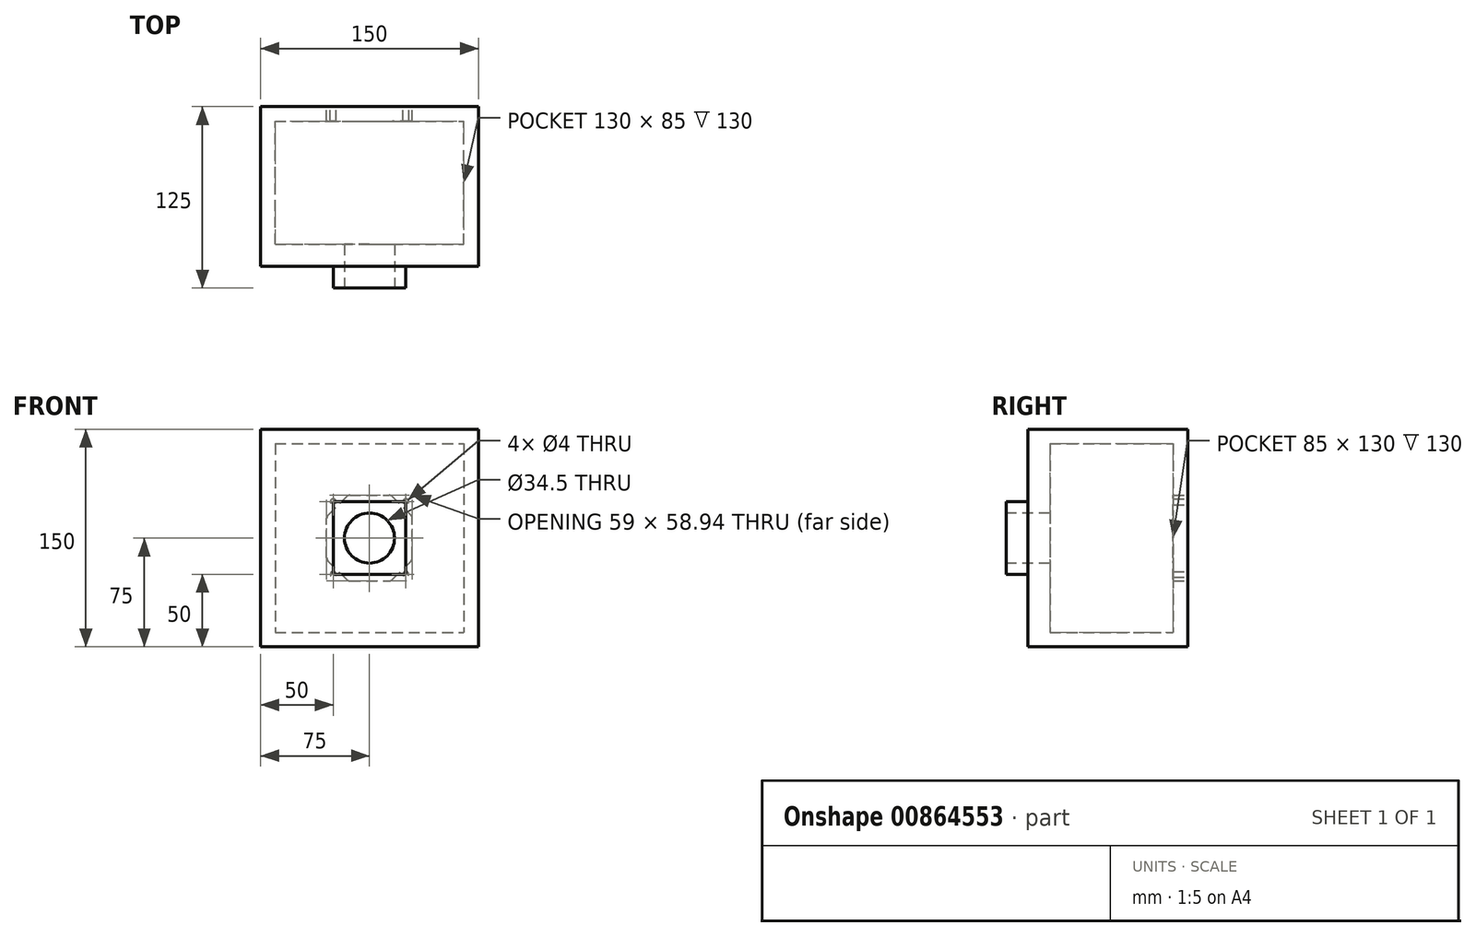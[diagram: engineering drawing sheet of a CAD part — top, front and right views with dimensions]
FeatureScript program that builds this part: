
annotation { "Feature Type Name" : "Feature", "Feature Type Description" : "" }
export const myFeature = defineFeature(function(context is Context, id is Id, definition is map)
    precondition{}
    {
        {
            var Q0;
            Q0=qCreatedBy(makeId("Front.planeOp"),FACE);
            var sketch = newSketch(context, id + "F0", { "sketchPlane" : qUnion([Q0])});
            skLineSegment(sketch, "E0", {"start": v(0, 165.5) * mm, "end": v(0, -188.76) * mm, "construction": true});
            skLineSegment(sketch, "E1", {"start": v(-193.08, 0) * mm, "end": v(189.02, 0) * mm, "construction": true});
            skLineSegment(sketch, "E2.bottom", {"start": v(-75, 75) * mm, "end": v(75, 75) * mm});
            skLineSegment(sketch, "E2.top", {"start": v(-75, -75) * mm, "end": v(75, -75) * mm});
            skLineSegment(sketch, "E2.left", {"start": v(-75, 75) * mm, "end": v(-75, -75) * mm});
            skLineSegment(sketch, "E2.right", {"start": v(75, 75) * mm, "end": v(75, -75) * mm});
            skSolve(sketch);
        }
        {
            var Q0;
            Q0 = qSketchRegion(id + "F0", true);
            extrude(context, id + "F1", {"entities" : qUnion([Q0]), "oppositeDirection" : true, "depth" : 100 * mm, "offsetDistance" : 25 * mm});
        }
        {
            var Q0;
            Q0=makeQuery(id+"F1.opExtrude","CAP_FACE",FACE,{"disambiguationData":[OSD([sQuery(id+"F0.wireOp",EDGE,"E2.bottom"),sQuery(id+"F0.wireOp",EDGE,"E2.top"),sQuery(id+"F0.wireOp",EDGE,"E2.left"),sQuery(id+"F0.wireOp",EDGE,"E2.right")])],"isStart":false});
            var sketch = newSketch(context, id + "F2", { "sketchPlane" : qUnion([Q0])});
            skLineSegment(sketch, "E3", {"start": v(0, 131.96) * mm, "end": v(0, -137.16) * mm, "construction": true});
            skLineSegment(sketch, "E4", {"start": v(-213.14, 0) * mm, "end": v(219.92, 0) * mm, "construction": true});
            skLineSegment(sketch, "E5.0", {"start": v(65, 65) * mm, "end": v(-65, 65) * mm});
            skLineSegment(sketch, "E5.1", {"start": v(65, 65) * mm, "end": v(65, -65) * mm});
            skLineSegment(sketch, "E5.2", {"start": v(65, -65) * mm, "end": v(-65, -65) * mm});
            skLineSegment(sketch, "E5.3", {"start": v(-65, 65) * mm, "end": v(-65, -65) * mm});
            skSolve(sketch);
        }
        {
            var Q0;
            Q0 = qSketchRegion(id + "F2", true);
            extrude(context, id + "F3", {"entities" : qUnion([Q0]), "operationType" : NewBodyOperationType.REMOVE, "oppositeDirection" : true, "depth" : 85 * mm, "offsetDistance" : 25 * mm});
        }
        {
            var Q0;
            Q0=makeQuery(id+"F1.opExtrude","CAP_FACE",FACE,{"disambiguationData":[OSD([sQuery(id+"F0.wireOp",EDGE,"E2.bottom"),sQuery(id+"F0.wireOp",EDGE,"E2.top"),sQuery(id+"F0.wireOp",EDGE,"E2.left"),sQuery(id+"F0.wireOp",EDGE,"E2.right")])],"isStart":false});
            var sketch = newSketch(context, id + "F4", { "sketchPlane" : qUnion([Q0])});
            skLineSegment(sketch, "E6.0", {"start": v(75, 75) * mm, "end": v(-75, 75) * mm});
            skLineSegment(sketch, "E6.1", {"start": v(-75, 75) * mm, "end": v(-75, -75) * mm});
            skLineSegment(sketch, "E6.2", {"start": v(75, -75) * mm, "end": v(-75, -75) * mm});
            skLineSegment(sketch, "E6.3", {"start": v(75, 75) * mm, "end": v(75, -75) * mm});
            skSolve(sketch);
        }
        {
            var Q0;
            Q0 = qSketchRegion(id + "F4", true);
            extrude(context, id + "F5", {"entities" : qUnion([Q0]), "operationType" : NewBodyOperationType.ADD, "depth" : 10 * mm, "offsetDistance" : 25 * mm});
        }
        {
            var Q0;
            Q0=makeQuery(id+"F1.opExtrude","CAP_FACE",FACE,{"disambiguationData":[OSD([sQuery(id+"F0.wireOp",EDGE,"E2.bottom"),sQuery(id+"F0.wireOp",EDGE,"E2.top"),sQuery(id+"F0.wireOp",EDGE,"E2.left"),sQuery(id+"F0.wireOp",EDGE,"E2.right")])],"isStart":true});
            var sketch = newSketch(context, id + "F6", { "sketchPlane" : qUnion([Q0])});
            skLineSegment(sketch, "E7", {"start": v(0, 53.92) * mm, "end": v(0, -52.12) * mm, "construction": true});
            skLineSegment(sketch, "E8", {"start": v(-54.18, 0) * mm, "end": v(61.76, 0) * mm, "construction": true});
            skLineSegment(sketch, "E9.bottom", {"start": v(-25, 25) * mm, "end": v(25, 25) * mm});
            skLineSegment(sketch, "E9.top", {"start": v(-25, -25) * mm, "end": v(25, -25) * mm});
            skLineSegment(sketch, "E9.left", {"start": v(-25, 25) * mm, "end": v(-25, -25) * mm});
            skLineSegment(sketch, "E9.right", {"start": v(25, 25) * mm, "end": v(25, -25) * mm});
            skSolve(sketch);
        }
        {
            var Q0;
            Q0 = qSketchRegion(id + "F6", true);
            extrude(context, id + "F7", {"entities" : qUnion([Q0]), "operationType" : NewBodyOperationType.ADD, "depth" : 15 * mm, "offsetDistance" : 25 * mm});
        }
        {
            var Q0;
            Q0=makeQuery(id+"F7.opExtrude","CAP_FACE",FACE,{"disambiguationData":[OSD([sQuery(id+"F6.wireOp",EDGE,"E9.bottom"),sQuery(id+"F6.wireOp",EDGE,"E9.top"),sQuery(id+"F6.wireOp",EDGE,"E9.left"),sQuery(id+"F6.wireOp",EDGE,"E9.right")])],"isStart":false});
            var sketch = newSketch(context, id + "F8", { "sketchPlane" : qUnion([Q0])});
            skCircle(sketch, "E10", {"center": v(0, 0) * mm, "radius": 17.25 * mm});
            skSolve(sketch);
        }
        {
            var Q0;
            Q0 = qSketchRegion(id + "F8", true);
            extrude(context, id + "F9", {"entities" : qUnion([Q0]), "operationType" : NewBodyOperationType.REMOVE, "endBound" : BoundingType.UP_TO_NEXT, "oppositeDirection" : true, "depth" : 25 * mm, "offsetDistance" : 25 * mm});
        }
        {
            var Q0;
            Q0=makeQuery(id+"F5.opExtrude","CAP_FACE",FACE,{"disambiguationData":[OSD([sQuery(id+"F4.wireOp",EDGE,"E6.0"),sQuery(id+"F4.wireOp",EDGE,"E6.1"),sQuery(id+"F4.wireOp",EDGE,"E6.2"),sQuery(id+"F4.wireOp",EDGE,"E6.3")])],"isStart":false});
            var sketch = newSketch(context, id + "F10", { "sketchPlane" : qUnion([Q0])});
            skLineSegment(sketch, "E11", {"start": v(0, 95.62) * mm, "end": v(0, -104.03) * mm, "construction": true});
            skLineSegment(sketch, "E12", {"start": v(-115.75, 0) * mm, "end": v(125.23, 0) * mm, "construction": true});
            skCircle(sketch, "E13", {"center": v(25, 25) * mm, "radius": 2 * mm});
            skCircle(sketch, "E14.MirrorC", {"center": v(25, -25) * mm, "radius": 2 * mm});
            skCircle(sketch, "E15.MirrorC", {"center": v(-25, 25) * mm, "radius": 2 * mm});
            skCircle(sketch, "E16.MirrorC", {"center": v(-25, -25) * mm, "radius": 2 * mm});
            skLineSegment(sketch, "E17", {"start": v(-14.85, 29.47) * mm, "end": v(14.85, 29.47) * mm, "construction": true});
            skLineSegment(sketch, "E18.MirrorCS", {"start": v(-14.85, -29.47) * mm, "end": v(14.85, -29.47) * mm, "construction": true});
            skLineSegment(sketch, "E19", {"start": v(-29.5, 14.85) * mm, "end": v(-29.5, -14.85) * mm, "construction": true});
            skLineSegment(sketch, "E20.MirrorCS", {"start": v(29.5, 14.85) * mm, "end": v(29.5, -14.85) * mm, "construction": true});
            skLineSegment(sketch, "E21", {"start": v(14.85, 29.47) * mm, "end": v(29.5, 14.85) * mm, "construction": true});
            skLineSegment(sketch, "E22", {"start": v(29.5, -14.85) * mm, "end": v(14.85, -29.47) * mm, "construction": true});
            skLineSegment(sketch, "E23", {"start": v(-14.85, 29.47) * mm, "end": v(-29.5, 14.85) * mm, "construction": true});
            skLineSegment(sketch, "E24", {"start": v(-29.5, -14.85) * mm, "end": v(-14.85, -29.47) * mm, "construction": true});
            skSolve(sketch);
        }
        {
            var Q0;
            Q0 = qSketchRegion(id + "F10", true);
            extrude(context, id + "F11", {"entities" : qUnion([Q0]), "operationType" : NewBodyOperationType.REMOVE, "endBound" : BoundingType.UP_TO_NEXT, "oppositeDirection" : true, "depth" : 25 * mm, "offsetDistance" : 25 * mm});
        }
        {
            var Q0;
            Q0=makeQuery(id+"F10.imprint","IMPRINT",FACE,{"disambiguationData":[TD([[makeQuery(id+"F10.imprint","IMPRINT",EDGE,{"derivedFrom":sQuery(id+"F10.wireOp",EDGE,"E13")}),-1.0]])]});
            var sketch = newSketch(context, id + "F12", { "sketchPlane" : qUnion([Q0])});
            skLineSegment(sketch, "E25.0", {"start": v(-14.85, 29.47) * mm, "end": v(14.85, 29.47) * mm});
            skLineSegment(sketch, "E26.0", {"start": v(-14.85, 29.47) * mm, "end": v(-29.5, 14.85) * mm});
            skLineSegment(sketch, "E26.1", {"start": v(-29.5, 14.85) * mm, "end": v(-29.5, -14.85) * mm});
            skLineSegment(sketch, "E26.2", {"start": v(-29.5, -14.85) * mm, "end": v(-14.85, -29.47) * mm});
            skLineSegment(sketch, "E26.3", {"start": v(-14.85, -29.47) * mm, "end": v(14.85, -29.47) * mm});
            skLineSegment(sketch, "E26.4", {"start": v(29.5, -14.85) * mm, "end": v(14.85, -29.47) * mm});
            skLineSegment(sketch, "E26.5", {"start": v(29.5, 14.85) * mm, "end": v(29.5, -14.85) * mm});
            skLineSegment(sketch, "E26.6", {"start": v(14.85, 29.47) * mm, "end": v(29.5, 14.85) * mm});
            skSolve(sketch);
        }
        {
            var Q0;
            Q0 = qSketchRegion(id + "F12", true);
            extrude(context, id + "F13", {"entities" : qUnion([Q0]), "operationType" : NewBodyOperationType.REMOVE, "endBound" : BoundingType.UP_TO_NEXT, "oppositeDirection" : true, "depth" : 25 * mm, "offsetDistance" : 25 * mm});
        }
        {
            var Q0;
            Q0=makeQuery(id+"F13.boolean.opBoolean","COPY",EDGE,{"derivedFrom":makeQuery(id+"F13.opExtrude","SWEPT_EDGE",EDGE,{"disambiguationData":[OSD([sQuery(id+"F12.wireOp",EDGE,"E26.0"),sQuery(id+"F12.wireOp",EDGE,"E26.1")])]})});
            var Q1;
            Q1=makeQuery(id+"F13.boolean.opBoolean","COPY",EDGE,{"derivedFrom":makeQuery(id+"F13.opExtrude","SWEPT_EDGE",EDGE,{"disambiguationData":[OSD([sQuery(id+"F12.wireOp",EDGE,"E25.0"),sQuery(id+"F12.wireOp",EDGE,"E26.0")])]})});
            var Q2;
            Q2=makeQuery(id+"F13.boolean.opBoolean","COPY",EDGE,{"derivedFrom":makeQuery(id+"F13.opExtrude","SWEPT_EDGE",EDGE,{"disambiguationData":[OSD([sQuery(id+"F12.wireOp",EDGE,"E26.1"),sQuery(id+"F12.wireOp",EDGE,"E26.2")])]})});
            var Q3;
            Q3=makeQuery(id+"F13.boolean.opBoolean","COPY",EDGE,{"derivedFrom":makeQuery(id+"F13.opExtrude","SWEPT_EDGE",EDGE,{"disambiguationData":[OSD([sQuery(id+"F12.wireOp",EDGE,"E26.2"),sQuery(id+"F12.wireOp",EDGE,"E26.3")])]})});
            var Q4;
            Q4=makeQuery(id+"F13.boolean.opBoolean","COPY",EDGE,{"derivedFrom":makeQuery(id+"F13.opExtrude","SWEPT_EDGE",EDGE,{"disambiguationData":[OSD([sQuery(id+"F12.wireOp",EDGE,"E26.3"),sQuery(id+"F12.wireOp",EDGE,"E26.4")])]})});
            var Q5;
            Q5=makeQuery(id+"F13.boolean.opBoolean","COPY",EDGE,{"derivedFrom":makeQuery(id+"F13.opExtrude","SWEPT_EDGE",EDGE,{"disambiguationData":[OSD([sQuery(id+"F12.wireOp",EDGE,"E25.0"),sQuery(id+"F12.wireOp",EDGE,"E26.6")])]})});
            var Q6;
            Q6=makeQuery(id+"F13.boolean.opBoolean","COPY",EDGE,{"derivedFrom":makeQuery(id+"F13.opExtrude","SWEPT_EDGE",EDGE,{"disambiguationData":[OSD([sQuery(id+"F12.wireOp",EDGE,"E26.5"),sQuery(id+"F12.wireOp",EDGE,"E26.6")])]})});
            var Q7;
            Q7=makeQuery(id+"F13.boolean.opBoolean","COPY",EDGE,{"derivedFrom":makeQuery(id+"F13.opExtrude","SWEPT_EDGE",EDGE,{"disambiguationData":[OSD([sQuery(id+"F12.wireOp",EDGE,"E26.4"),sQuery(id+"F12.wireOp",EDGE,"E26.5")])]})});
            fillet(context, id + "F14", {"entities" : qUnion([Q0, Q1, Q2, Q3, Q4, Q5, Q6, Q7]), "radius" : 3 * mm, "tangentPropagation" : true, "allowEdgeOverflow" : false});
        }
    });
